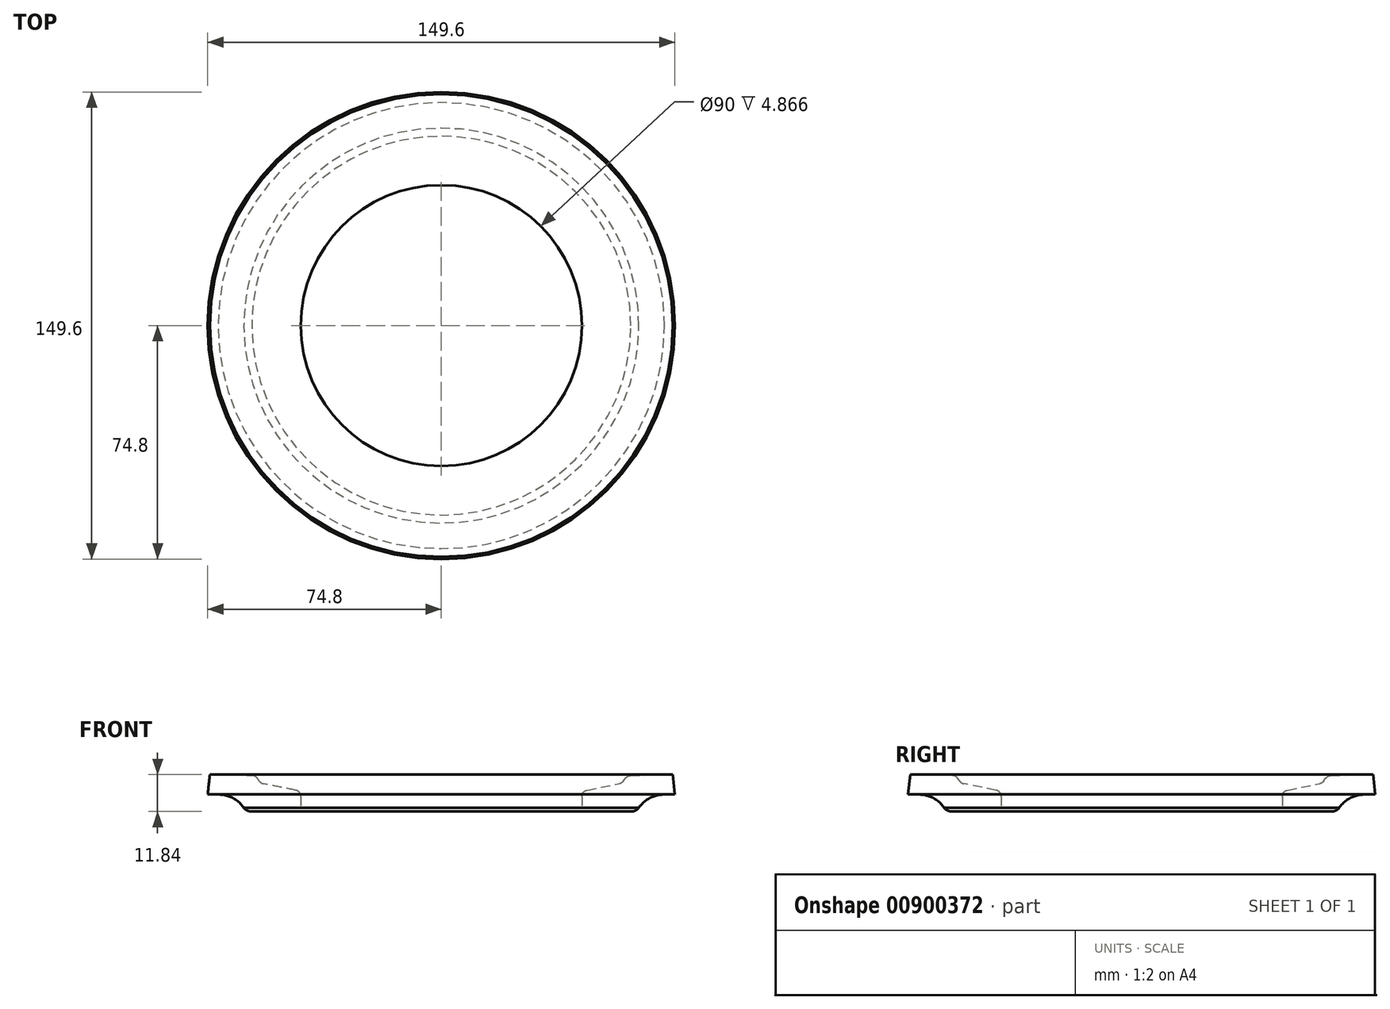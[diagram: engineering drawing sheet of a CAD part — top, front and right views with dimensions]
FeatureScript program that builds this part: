
annotation { "Feature Type Name" : "Feature", "Feature Type Description" : "" }
export const myFeature = defineFeature(function(context is Context, id is Id, definition is map)
    precondition{}
    {
        {
            var Q0;
            Q0=qCreatedBy(makeId("Front.planeOp"),FACE);
            var sketch = newSketch(context, id + "F0", { "sketchPlane" : qUnion([Q0])});
            skLineSegment(sketch, "E0", {"start": v(0, 0) * mm, "end": v(0, 4.87) * mm});
            skLineSegment(sketch, "E1", {"start": v(12, 8.88) * mm, "end": v(1.61, 6.83) * mm});
            skLineSegment(sketch, "E2", {"start": v(13.94, 10.65) * mm, "end": v(13.22, 9.66) * mm});
            skLineSegment(sketch, "E3", {"start": v(29.11, 11.83) * mm, "end": v(15.5, 11.48) * mm});
            skPoint(sketch, "E4.visualSharp", {"position": v(0, 6.5) * mm});
            skArc(sketch, "E4.filletArc", {"start": v(1.61, 6.83) * mm, "mid": v(0.45, 6.14) * mm, "end": v(0, 4.87) * mm});
            skPoint(sketch, "E5.visualSharp", {"position": v(12.76, 9.03) * mm});
            skArc(sketch, "E5.filletArc", {"start": v(12, 8.88) * mm, "mid": v(12.68, 9.15) * mm, "end": v(13.22, 9.66) * mm});
            skPoint(sketch, "E6.visualSharp", {"position": v(14.52, 11.45) * mm});
            skArc(sketch, "E6.filletArc", {"start": v(15.5, 11.48) * mm, "mid": v(14.63, 11.25) * mm, "end": v(13.94, 10.65) * mm});
            skLineSegment(sketch, "E7", {"start": v(0, 0) * mm, "end": v(15.84, 0) * mm});
            skLineSegment(sketch, "E8", {"start": v(15.84, 0) * mm, "end": v(15.84, 3) * mm});
            skLineSegment(sketch, "E9", {"start": v(15.84, 3) * mm, "end": v(19.86, 3) * mm});
            skLineSegment(sketch, "E10", {"start": v(19.86, 3) * mm, "end": v(19.86, 3) * mm});
            skArc(sketch, "E11", {"start": v(26.44, 5.46) * mm, "mid": v(21.82, 4.33) * mm, "end": v(18.25, 1.2) * mm});
            skLineSegment(sketch, "E12", {"start": v(19.86, 3) * mm, "end": v(19.86, 5.47) * mm});
            skLineSegment(sketch, "E13", {"start": v(26.44, -4.55) * mm, "end": v(26.44, 5.46) * mm});
            skLineSegment(sketch, "E14", {"start": v(29.8, 5.5) * mm, "end": v(26.44, 5.46) * mm});
            skArc(sketch, "E15", {"start": v(18.84, 3) * mm, "mid": v(12.97, 3.88) * mm, "end": v(18.33, 1.31) * mm});
            skLineSegment(sketch, "E16", {"start": v(29.11, 11.83) * mm, "end": v(29.8, 5.5) * mm});
            skLineSegment(sketch, "E17", {"start": v(0, 0) * mm, "end": v(-45, 0) * mm});
            skSolve(sketch);
        }
        {
            var Q0;
            Q0=qCreatedBy(makeId("Top.planeOp"),FACE);
            var sketch = newSketch(context, id + "F1", { "sketchPlane" : qUnion([Q0])});
            skLineSegment(sketch, "E18", {"start": v(0, 0) * mm, "end": v(-45, 0) * mm});
            skCircle(sketch, "E19", {"center": v(-45, 0) * mm, "radius": 45 * mm});
            skSolve(sketch);
        }
        {
            var Q0;
            {var subQ1=sQuery(id+"F0.wireOp",EDGE,"E0");Q0=makeQuery(id+"F0.imprint","IMPRINT",FACE,{"disambiguationData":[TD([[makeQuery(id+"F0.imprint","IMPRINT",EDGE,{"derivedFrom":subQ1}),-1.0]])]});}
            var Q1;
            {var subQ4=sQuery(id+"F0.wireOp",EDGE,"E8");Q1=makeQuery(id+"F0.imprint","IMPRINT",FACE,{"disambiguationData":[TD([[makeQuery(id+"F0.imprint","IMPRINT",EDGE,{"derivedFrom":subQ4}),-1.0]])]});}
            var Q2;
            {var subQ0=sQuery(id+"F0.wireOp",EDGE,"E8");Q2=makeQuery(id+"F0.imprint","IMPRINT",FACE,{"disambiguationData":[TD([[makeQuery(id+"F0.imprint","IMPRINT",EDGE,{"derivedFrom":subQ0}),1.0]])]});}
            var Q3;
            Q3=sQuery(id+"F1.wireOp",EDGE,"E19");
            revolve(context, id + "F2", {"surfaceOperationType" : NewSurfaceOperationType.NEW, "entities" : qUnion([Q0, Q1, Q2]), "axis" : qUnion([Q3]), "revolveType" : RevolveType.FULL});
        }
    });
